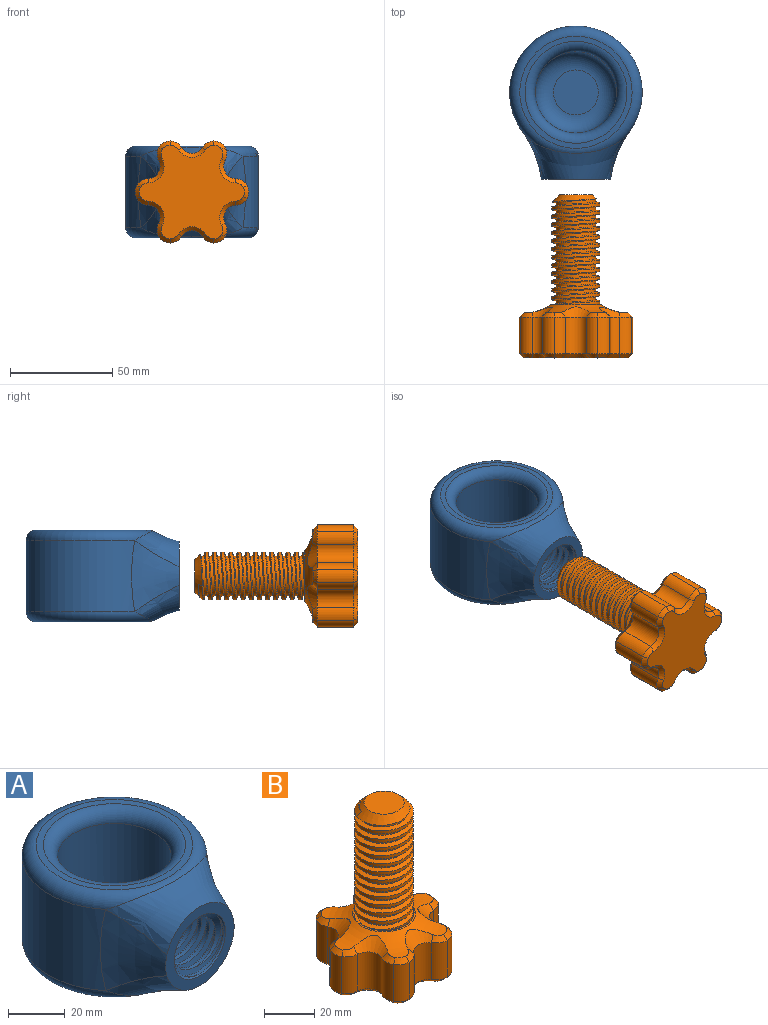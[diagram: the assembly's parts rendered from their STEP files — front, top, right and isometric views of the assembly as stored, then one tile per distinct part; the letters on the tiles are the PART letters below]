
ASSEMBLY  parts=2 mates=1
PART A: 25 faces, bbox 70.8x78.1x45.4 mm
  f0: cylinder r=12.25mm len=24.5mm, axis (0,-1,0), area 658.3mm2, adj f2,f3,f12,f19
  f1: cylinder r=10.25mm len=21.03mm, axis (0,1,0), area 499.5mm2, adj f2,f3,f12,f14,f19,f20
  f2: bspline ~24.47x24.42mm, area 816.1mm2, adj f0,f1,f10,f12,f19
  f3: bspline ~28.29x24.52mm, area 815.8mm2, adj f0,f1,f7,f12,f14,f19,f20
  f4: plane 55x55mm, normal (0,0,1), area 412.3mm2, adj f15,f17
  f5: plane 55x55mm, normal (0,0,-1), area 2375.8mm2, adj f16
  f6: cylinder r=12.25mm len=12.57mm, axis (0,-1,0), area 0mm2, adj f8,f12
  f7: cylinder r=10.25mm len=16.86mm, axis (0,1,0), area 20.7mm2, adj f3,f8,f12,f14
  f8: bspline ~18.38x14.15mm, area 21mm2, adj f6,f7,f12
  f9: bspline ~24.5x14.15mm, area 0mm2, adj f10,f12
  f10: cylinder r=12.25mm len=21.5mm, axis (0,-1,0), area 33mm2, adj f2,f9,f12
  f11: plane 34.4x34.4mm, normal (0,-1,0), area 394.6mm2, adj f19,f21,f22,f23,f24
  f12: cylinder r=20mm len=40mm, axis (0,0,1), area 2984.8mm2, adj f0,f1,f2,f3,f6,f7,f8,f9
  f13: plane 22x22mm, normal (0,0,1), area 380.1mm2, adj f14
  f14: torus R=11mm, axis (0,0,1), area 1482mm2, adj f1,f3,f7,f12,f13
  f15: torus R=25mm, axis (0,0,1), area 1076.6mm2, adj f4,f12
  f16: torus R=27.5mm, axis (0,0,1), area 1308.7mm2, adj f5,f18,f21
  f17: torus R=27.5mm, axis (0,0,1), area 1308.7mm2, adj f4,f18,f24
  f18: cylinder r=32.5mm len=65mm, axis (0,0,1), area 5053mm2, adj f16,f17,f22,f23
  f19: cone r=14.78mm half-angle=45deg, axis (0,-1,0), area 159.9mm2, adj f0,f1,f2,f3,f11,f20
  f20: cone r=14.78mm half-angle=45deg, axis (0,-1,0), area 0mm2, adj f1,f3,f19
  f21: bspline ~50.13x21.81mm, area 810.7mm2, adj f11,f16,f22,f23
  f22: bspline ~35x23.33mm, area 556.7mm2, adj f11,f18,f21,f24
  f23: bspline ~35x23.33mm, area 556.7mm2, adj f11,f18,f21,f24
  f24: bspline ~50.13x21.81mm, area 810.7mm2, adj f11,f17,f22,f23
PART B: 83 faces, bbox 56.2x56.2x80.3 mm
  f0: plane 24.24x24.24mm, normal (0,0,1), area 83.6mm2, adj f1,f2,f3,f4,f82
  f1: cylinder r=11.75mm len=50.25mm, axis (0,0,-1), area 1552mm2, adj f0,f3,f4,f6
  f2: cylinder r=9.75mm len=52.25mm, axis (0,0,1), area 1664.7mm2, adj f0,f3,f4,f5
  f3: bspline ~53.85x27.14mm, area 1784.4mm2, adj f0,f1,f2,f5,f6
  f4: bspline ~53.18x27.14mm, area 1796.8mm2, adj f0,f1,f2,f6
  f5: cone r=6mm half-angle=45deg, axis (0,0,-1), area 196.4mm2, adj f2,f3,f6,f7
  f6: cone r=6mm half-angle=45deg, axis (0,0,-1), area 36.4mm2, adj f1,f3,f4,f5
  f7: plane 16x16mm, normal (0,0,1), area 201.1mm2, adj f5
  f8: cylinder r=6mm len=18mm, axis (0,0,-1), area 216.5mm2, adj f18,f30,f42,f63
  f9: cylinder r=6mm len=18mm, axis (0,0,-1), area 216.5mm2, adj f27,f32,f34,f58
  f10: cylinder r=6mm len=18mm, axis (0,0,-1), area 216.5mm2, adj f24,f29,f39,f66
  f11: cylinder r=6mm len=18mm, axis (0,0,-1), area 216.5mm2, adj f21,f26,f47,f74
  f12: cylinder r=6mm len=18mm, axis (0,0,-1), area 216.5mm2, adj f15,f23,f55,f79
  f13: cylinder r=6mm len=18mm, axis (0,0,-1), area 216.5mm2, adj f17,f20,f50,f71
  f14: plane 51.57x45.98mm, normal (0,0,-1), area 1392.8mm2, adj f57,f58,f59,f60,f61,f62,f63,f64
  f15: cylinder r=7mm len=18mm, axis (0,0,-1), area 121.2mm2, adj f12,f16,f56,f77
  f16: cylinder r=7mm len=18mm, axis (0,0,-1), area 121.8mm2, adj f15,f17,f54,f75
  f17: cylinder r=7mm len=18mm, axis (0,0,-1), area 121.2mm2, adj f13,f16,f52,f73
  f18: cylinder r=7mm len=18mm, axis (0,0,-1), area 121.2mm2, adj f8,f19,f44,f65
  f19: cylinder r=7mm len=18mm, axis (0,0,-1), area 121.8mm2, adj f18,f20,f46,f67
  f20: cylinder r=7mm len=18mm, axis (0,0,-1), area 121.2mm2, adj f13,f19,f48,f69
  f21: cylinder r=7mm len=18mm, axis (0,0,-1), area 121.2mm2, adj f11,f22,f49,f76
  f22: cylinder r=7mm len=18mm, axis (0,0,-1), area 121.8mm2, adj f21,f23,f51,f78
  f23: cylinder r=7mm len=18mm, axis (0,0,-1), area 121.2mm2, adj f12,f22,f53,f80
  f24: cylinder r=7mm len=18mm, axis (0,0,-1), area 121.2mm2, adj f10,f25,f41,f68
  f25: cylinder r=7mm len=18mm, axis (0,0,-1), area 121.8mm2, adj f24,f26,f43,f70
  f26: cylinder r=7mm len=18mm, axis (0,0,-1), area 121.2mm2, adj f11,f25,f45,f72
  f27: cylinder r=7mm len=18mm, axis (0,0,-1), area 121.2mm2, adj f9,f28,f33,f60
  f28: cylinder r=7mm len=18mm, axis (0,0,-1), area 121.8mm2, adj f27,f29,f35,f62
  f29: cylinder r=7mm len=18mm, axis (0,0,-1), area 121.2mm2, adj f10,f28,f37,f64
  f30: cylinder r=7mm len=18mm, axis (0,0,-1), area 121.2mm2, adj f8,f31,f40,f61
  f31: cylinder r=7mm len=18mm, axis (0,0,-1), area 121.8mm2, adj f30,f32,f38,f59
  f32: cylinder r=7mm len=18mm, axis (0,0,-1), area 121.2mm2, adj f9,f31,f36,f57
  f33: cone r=5mm half-angle=45deg, axis (0,0,-1), area 17.3mm2, adj f27,f34,f35,f81
  f34: cone r=8mm half-angle=45deg, axis (0,0,1), area 80.3mm2, adj f9,f33,f36,f81
  f35: cone r=5mm half-angle=45deg, axis (0,0,-1), area 16.2mm2, adj f28,f33,f37,f81
  f36: cone r=5mm half-angle=45deg, axis (0,0,-1), area 17.3mm2, adj f32,f34,f38,f81
  f37: cone r=5mm half-angle=45deg, axis (0,0,-1), area 17.3mm2, adj f29,f35,f39,f81
  f38: cone r=5mm half-angle=45deg, axis (0,0,-1), area 16.2mm2, adj f31,f36,f40,f81
  f39: cone r=8mm half-angle=45deg, axis (0,0,1), area 80.3mm2, adj f10,f37,f41,f81
  f40: cone r=5mm half-angle=45deg, axis (0,0,-1), area 17.3mm2, adj f30,f38,f42,f81
  f41: cone r=5mm half-angle=45deg, axis (0,0,-1), area 17.3mm2, adj f24,f39,f43,f81
  f42: cone r=8mm half-angle=45deg, axis (0,0,1), area 80.3mm2, adj f8,f40,f44,f81
  f43: cone r=5mm half-angle=45deg, axis (0,0,-1), area 16.2mm2, adj f25,f41,f45,f81
  f44: cone r=5mm half-angle=45deg, axis (0,0,-1), area 17.3mm2, adj f18,f42,f46,f81
  f45: cone r=5mm half-angle=45deg, axis (0,0,-1), area 17.3mm2, adj f26,f43,f47,f81
  f46: cone r=5mm half-angle=45deg, axis (0,0,-1), area 16.2mm2, adj f19,f44,f48,f81
  f47: cone r=8mm half-angle=45deg, axis (0,0,1), area 80.3mm2, adj f11,f45,f49,f81
  f48: cone r=5mm half-angle=45deg, axis (0,0,-1), area 17.3mm2, adj f20,f46,f50,f81
  f49: cone r=5mm half-angle=45deg, axis (0,0,-1), area 17.3mm2, adj f21,f47,f51,f81
  f50: cone r=8mm half-angle=45deg, axis (0,0,1), area 80.3mm2, adj f13,f48,f52,f81
  f51: cone r=5mm half-angle=45deg, axis (0,0,-1), area 16.2mm2, adj f22,f49,f53,f81
  f52: cone r=5mm half-angle=45deg, axis (0,0,-1), area 17.3mm2, adj f17,f50,f54,f81
  f53: cone r=5mm half-angle=45deg, axis (0,0,-1), area 17.3mm2, adj f23,f51,f55,f81
  f54: cone r=5mm half-angle=45deg, axis (0,0,-1), area 16.2mm2, adj f16,f52,f56,f81
  f55: cone r=8mm half-angle=45deg, axis (0,0,1), area 80.3mm2, adj f12,f53,f56,f81
  f56: cone r=5mm half-angle=45deg, axis (0,0,-1), area 17.3mm2, adj f15,f54,f55,f81
  f57: cone r=5mm half-angle=45deg, axis (0,0,1), area 16.2mm2, adj f14,f32,f58,f59
  f58: cone r=6mm half-angle=45deg, axis (0,0,-1), area 39.7mm2, adj f9,f14,f57,f60
  f59: cone r=5mm half-angle=45deg, axis (0,0,1), area 16.2mm2, adj f14,f31,f57,f61
  f60: cone r=5mm half-angle=45deg, axis (0,0,1), area 16.2mm2, adj f14,f27,f58,f62
  f61: cone r=5mm half-angle=45deg, axis (0,0,1), area 16.2mm2, adj f14,f30,f59,f63
  f62: cone r=5mm half-angle=45deg, axis (0,0,1), area 16.2mm2, adj f14,f28,f60,f64
  f63: cone r=6mm half-angle=45deg, axis (0,0,-1), area 39.7mm2, adj f8,f14,f61,f65
  f64: cone r=5mm half-angle=45deg, axis (0,0,1), area 16.2mm2, adj f14,f29,f62,f66
  f65: cone r=5mm half-angle=45deg, axis (0,0,1), area 16.2mm2, adj f14,f18,f63,f67
  f66: cone r=6mm half-angle=45deg, axis (0,0,-1), area 39.7mm2, adj f10,f14,f64,f68
  f67: cone r=5mm half-angle=45deg, axis (0,0,1), area 16.2mm2, adj f14,f19,f65,f69
  f68: cone r=5mm half-angle=45deg, axis (0,0,1), area 16.2mm2, adj f14,f24,f66,f70
  f69: cone r=5mm half-angle=45deg, axis (0,0,1), area 16.2mm2, adj f14,f20,f67,f71
  f70: cone r=5mm half-angle=45deg, axis (0,0,1), area 16.2mm2, adj f14,f25,f68,f72
  f71: cone r=6mm half-angle=45deg, axis (0,0,-1), area 39.7mm2, adj f13,f14,f69,f73
  f72: cone r=5mm half-angle=45deg, axis (0,0,1), area 16.2mm2, adj f14,f26,f70,f74
  f73: cone r=5mm half-angle=45deg, axis (0,0,1), area 16.2mm2, adj f14,f17,f71,f75
  f74: cone r=6mm half-angle=45deg, axis (0,0,-1), area 39.7mm2, adj f11,f14,f72,f76
  f75: cone r=5mm half-angle=45deg, axis (0,0,1), area 16.2mm2, adj f14,f16,f73,f77
  f76: cone r=5mm half-angle=45deg, axis (0,0,1), area 16.2mm2, adj f14,f21,f74,f78
  f77: cone r=5mm half-angle=45deg, axis (0,0,1), area 16.2mm2, adj f14,f15,f75,f79
  f78: cone r=5mm half-angle=45deg, axis (0,0,1), area 16.2mm2, adj f14,f22,f76,f80
  f79: cone r=6mm half-angle=45deg, axis (0,0,-1), area 39.7mm2, adj f12,f14,f77,f80
  f80: cone r=5mm half-angle=45deg, axis (0,0,1), area 16.2mm2, adj f14,f23,f78,f79
  f81: torus R=25.81mm, axis (0,0,1), area 772.5mm2, adj f33,f34,f35,f36,f37,f38,f39,f40
  f82: torus R=11.96mm, axis (0,0,-1), area 43.2mm2, adj f0,f81
PLACE A t=(-23.55,-49.67,-130.59)mm
PLACE B rot(axis=(-1,0,0),90deg) t=(-23.55,-169.79,-108.09)mm
MATE slider A.f0 <-> B.f1  axis (0,1,0) through (-23.55,-69.52,-108.09)mm
